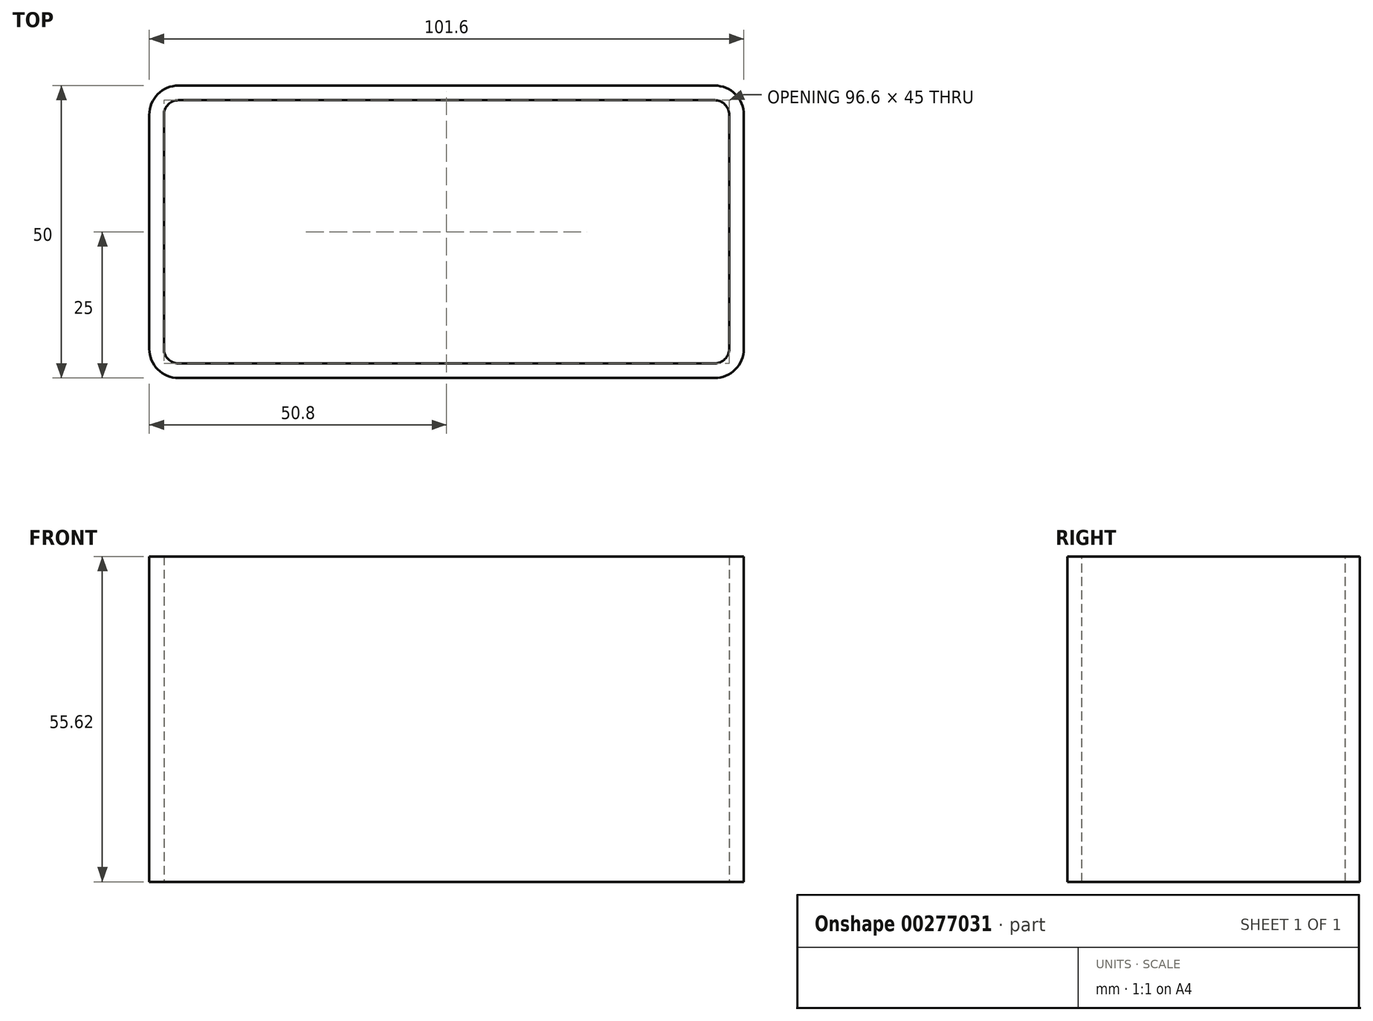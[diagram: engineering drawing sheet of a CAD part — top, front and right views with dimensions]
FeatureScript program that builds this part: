
annotation { "Feature Type Name" : "Feature", "Feature Type Description" : "" }
export const myFeature = defineFeature(function(context is Context, id is Id, definition is map)
    precondition{}
    {
        {
            var Q0;
            Q0=qCreatedBy(makeId("Front.planeOp"),FACE);
            var sketch = newSketch(context, id + "F0", { "sketchPlane" : qUnion([Q0])});
            skLineSegment(sketch, "E0.bottom", {"start": v(-50.8, 27.81) * mm, "end": v(50.8, 27.81) * mm});
            skLineSegment(sketch, "E0.top", {"start": v(-50.8, -27.81) * mm, "end": v(50.8, -27.81) * mm});
            skLineSegment(sketch, "E0.left", {"start": v(-50.8, 27.81) * mm, "end": v(-50.8, -27.81) * mm});
            skLineSegment(sketch, "E0.right", {"start": v(50.8, 27.81) * mm, "end": v(50.8, -27.81) * mm});
            skPoint(sketch, "E0.middle", {"position": v(0, 0) * mm});
            skSolve(sketch);
        }
        {
            var Q0;
            Q0=makeQuery(id+"F0.imprint","IMPRINT",FACE,{"disambiguationData":[TD([[makeQuery(id+"F0.imprint","IMPRINT",EDGE,{"derivedFrom":sQuery(id+"F0.wireOp",EDGE,"E0.bottom")}),-1.0]])]});
            extrude(context, id + "F1", {"entities" : qUnion([Q0]), "depth" : 50 * mm});
        }
        {
            var Q0;
            Q0=makeQuery(id+"F1.opExtrude","CAP_EDGE",EDGE,{"disambiguationData":[OSD([sQuery(id+"F0.wireOp",EDGE,"E0.left")])],"isStart":false});
            var Q1;
            Q1=makeQuery(id+"F1.opExtrude","CAP_EDGE",EDGE,{"disambiguationData":[OSD([sQuery(id+"F0.wireOp",EDGE,"E0.right")])],"isStart":false});
            var Q2;
            Q2=makeQuery(id+"F1.opExtrude","CAP_EDGE",EDGE,{"disambiguationData":[OSD([sQuery(id+"F0.wireOp",EDGE,"E0.right")])],"isStart":true});
            var Q3;
            Q3=makeQuery(id+"F1.opExtrude","CAP_EDGE",EDGE,{"disambiguationData":[OSD([sQuery(id+"F0.wireOp",EDGE,"E0.left")])],"isStart":true});
            fillet(context, id + "F2", {"entities" : qUnion([Q0, Q1, Q2, Q3]), "radius" : 5 * mm, "tangentPropagation" : true, "allowEdgeOverflow" : false});
        }
        {
            var Q0;
            Q0=makeQuery(id+"F1.opExtrude","SWEPT_FACE",FACE,{"disambiguationData":[OSD([sQuery(id+"F0.wireOp",EDGE,"E0.bottom")])]});
            var Q1;
            Q1=makeQuery(id+"F1.opExtrude","SWEPT_FACE",FACE,{"disambiguationData":[OSD([sQuery(id+"F0.wireOp",EDGE,"E0.top")])]});
            shell(context, id + "F3", {"entities" : qUnion([Q0, Q1]), "thickness" : 2.5 * mm});
        }
    });
